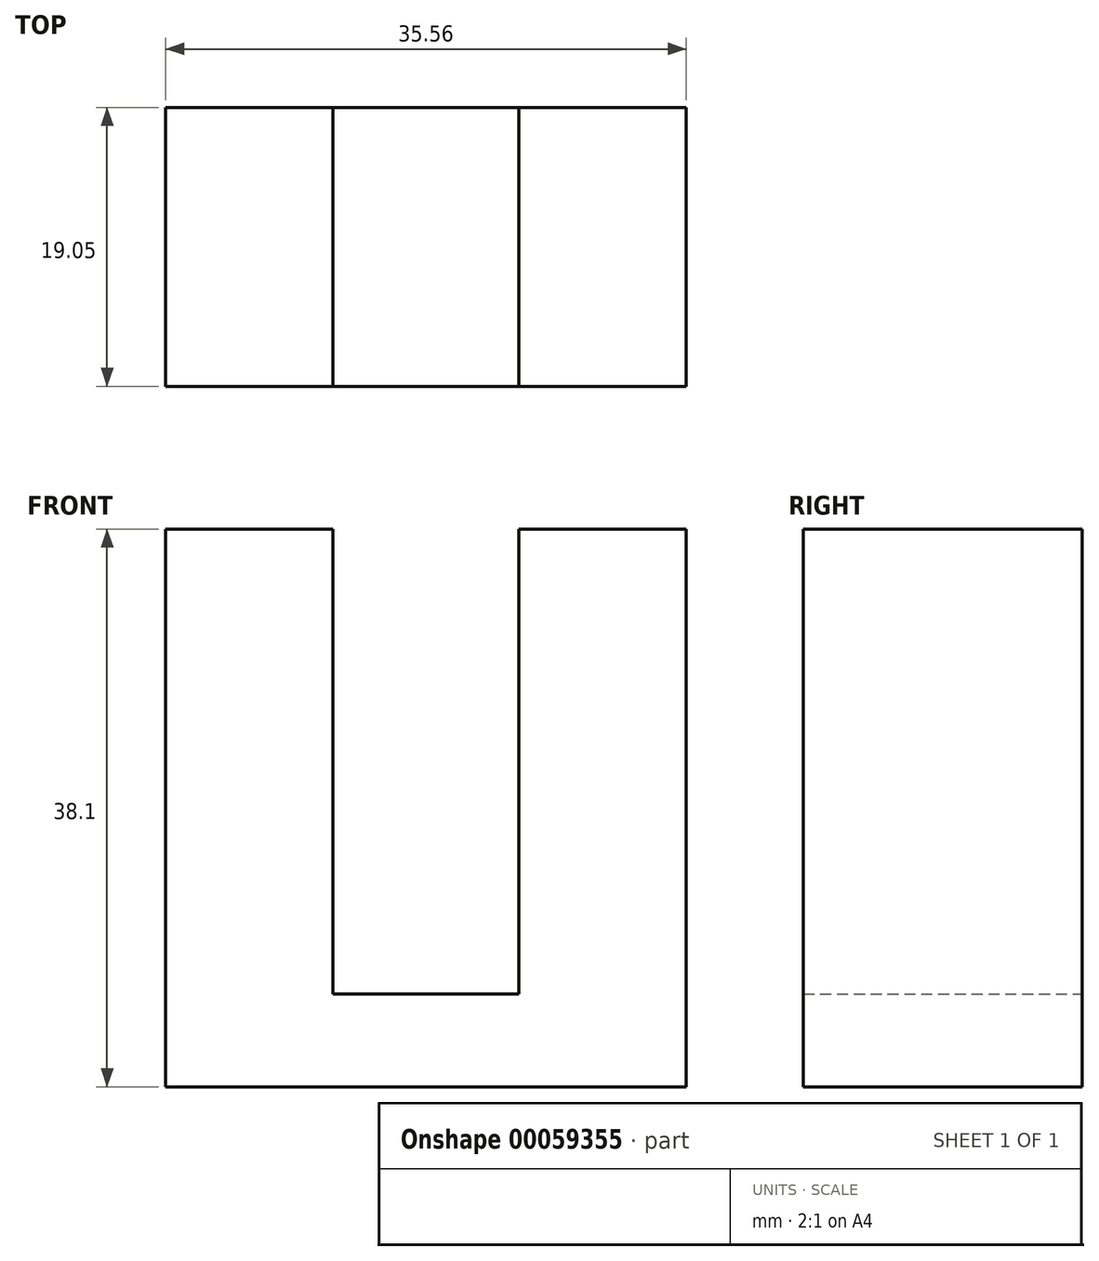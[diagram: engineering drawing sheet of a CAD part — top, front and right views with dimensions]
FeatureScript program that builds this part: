
annotation { "Feature Type Name" : "Feature", "Feature Type Description" : "" }
export const myFeature = defineFeature(function(context is Context, id is Id, definition is map)
    precondition{}
    {
        {
            var Q0;
            Q0=qCreatedBy(makeId("Front.planeOp"),FACE);
            var sketch = newSketch(context, id + "F0", { "sketchPlane" : qUnion([Q0])});
            skLineSegment(sketch, "E0", {"start": v(-17.78, 28.75) * mm, "end": v(-17.78, -9.35) * mm});
            skLineSegment(sketch, "E1", {"start": v(-17.78, -9.35) * mm, "end": v(17.78, -9.35) * mm});
            skLineSegment(sketch, "E2", {"start": v(17.78, -9.35) * mm, "end": v(17.78, 28.75) * mm});
            skLineSegment(sketch, "E3", {"start": v(17.78, 28.75) * mm, "end": v(6.35, 28.75) * mm});
            skLineSegment(sketch, "E4", {"start": v(6.35, 28.75) * mm, "end": v(6.35, -3) * mm});
            skLineSegment(sketch, "E5", {"start": v(6.35, -3) * mm, "end": v(-6.35, -3) * mm});
            skLineSegment(sketch, "E6", {"start": v(-6.35, -3) * mm, "end": v(-6.35, 28.75) * mm});
            skLineSegment(sketch, "E7", {"start": v(-6.35, 28.75) * mm, "end": v(-17.78, 28.75) * mm});
            skSolve(sketch);
        }
        {
            var Q0;
            Q0=makeQuery(id+"F0.imprint","IMPRINT",FACE,{"disambiguationData":[TD([[makeQuery(id+"F0.imprint","IMPRINT",EDGE,{"derivedFrom":sQuery(id+"F0.wireOp",EDGE,"E0")}),1.0]])]});
            extrude(context, id + "F1", {"entities" : qUnion([Q0]), "depth" : 19.05 * mm});
        }
    });
